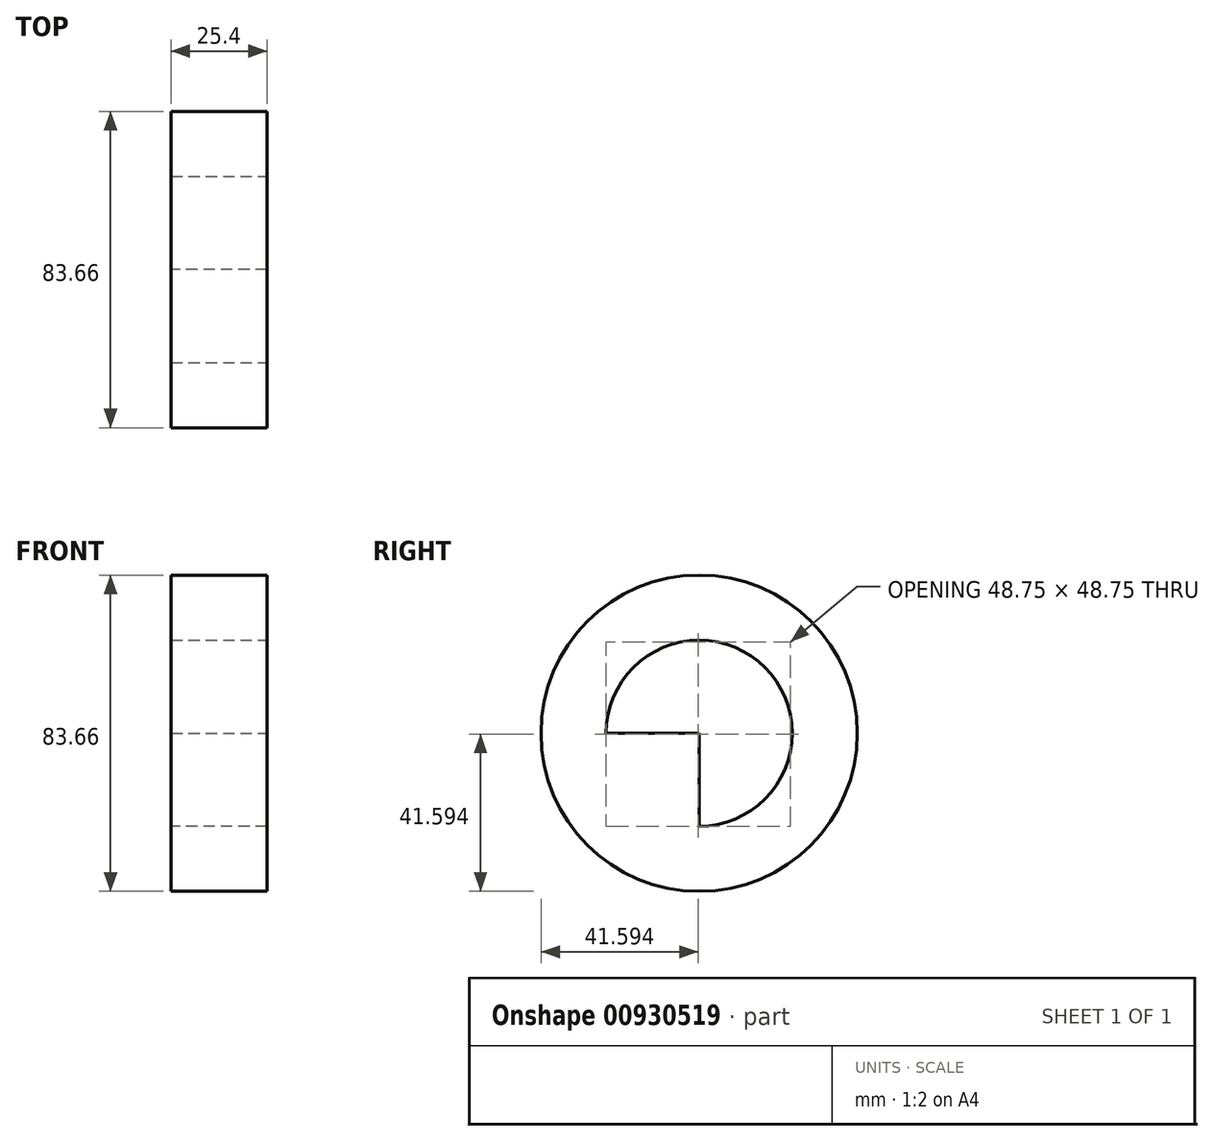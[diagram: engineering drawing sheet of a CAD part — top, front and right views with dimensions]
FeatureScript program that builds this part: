
annotation { "Feature Type Name" : "Feature", "Feature Type Description" : "" }
export const myFeature = defineFeature(function(context is Context, id is Id, definition is map)
    precondition{}
    {
        {
            var Q0;
            Q0=qCreatedBy(makeId("Right.planeOp"),FACE);
            var sketch = newSketch(context, id + "F0", { "sketchPlane" : qUnion([Q0])});
            skLineSegment(sketch, "E0.bottom", {"start": v(0, 0) * mm, "end": v(-33.83, 0) * mm});
            skLineSegment(sketch, "E0.top", {"start": v(0, -24.61) * mm, "end": v(-33.83, -24.61) * mm});
            skLineSegment(sketch, "E0.left", {"start": v(0, 0) * mm, "end": v(0, -24.61) * mm});
            skLineSegment(sketch, "E0.right", {"start": v(-33.83, 0) * mm, "end": v(-33.83, -24.61) * mm});
            skSolve(sketch);
        }
        {
            var Q0;
            Q0=makeQuery(id+"F0.imprint","IMPRINT",FACE,{"disambiguationData":[TD([[makeQuery(id+"F0.imprint","IMPRINT",EDGE,{"derivedFrom":sQuery(id+"F0.wireOp",EDGE,"E0.bottom")}),1.0]])]});
            extrude(context, id + "F1", {"entities" : qUnion([Q0]), "depth" : 25.4 * mm, "offsetDistance" : 25.4 * mm});
        }
        {
            var Q0;
            Q0=makeQuery(id+"F1.opExtrude","SWEPT_FACE",FACE,{"disambiguationData":[OSD([sQuery(id+"F0.wireOp",EDGE,"E0.top")])]});
            var Q1;
            Q1=makeQuery(id+"F1.opExtrude","SWEPT_EDGE",EDGE,{"disambiguationData":[OSD([sQuery(id+"F0.wireOp",EDGE,"E0.bottom"),sQuery(id+"F0.wireOp",EDGE,"E0.left")])]});
            revolve(context, id + "F2", {"operationType" : NewBodyOperationType.ADD, "surfaceOperationType" : NewSurfaceOperationType.NEW, "entities" : qUnion([Q0]), "axis" : qUnion([Q1]), "revolveType" : RevolveType.FULL});
        }
    });
